# Revit family: BC_Hitachi_RASC-HNpE_LOD200
name_source: partatom
category: Equipement de génie climatique
revit_build: Autodesk Revit 2016 (Build: 20150220_1215(x64)
units: mm (PartAtom-declared; Revit-internal decimal feet)

## family parameters
Basée sur le plan de construction = Non
Cote de connecteur circulaire = Utiliser le diamètre
Couper avec des vides une fois chargée = Non
Numéro OmniClass = 23.75.00.00
Partagée = Non
Point de calcul de pièce = Non
Titre OmniClass = Climate Control (HVAC)
Toujours verticalement = Oui
Type d'élément = Normal

## types (5) — shared parameters
Description = Centrifugal VRF Series RASC-HNPE
Fabricant = HITACHI
Frequency = 50 Hz
Maximum AC Voltage = 440 V
Maximum Connected Capacity (%) = 120
Minimum AC Voltage = 360 V
Minimum Connected Capacity (%) = 75
Modèle = Outdoor Unit - Centrifugal RASC-HNPE
Nominal Voltage = 400 V
Number of Poles = 3
Refrigerant = R410A

## per-type parameters (varying)
- RASC-4HNPE: Coefficient Of Performance (COP)=3.8; Cooling Capacity=10 kW; Distance from left outlet=123 mm; ESEER=6.65; Energy Efficiency Ratio (EER)=3.35; Gas Diameter=16 mm; Heating Capacity=11 kW; Height Gas pipe=439 mm; Height liquid pipe=319 mm; Input Height=444 mm; Input Width=642 mm; Liquid Diameter=10 mm  [stored 0.0328084 ft]; Mass=192.00 kg; Maximum Air Flow=55000.0 L/min; Maximum Input Power=9 kW; Nominal Current=14 A; Nominal cooling power input=3 kW; Nominal heating power input=3 kW; Output Height=288 mm; Output Width=334 mm; Overall Depth=1015 mm; Overall Height=575 mm; Overall Width=1415 mm; Product Code=7E343107; Recommended circuit breaker=20 A; Refrigerant charge=4.10 kg; Running current cooling=5 A; Running current heating=5 A; Sound power dB(A)=70; Sound pressure level Night mode cooling (dB(A))=48; Sound pressure level cooling (dB(A))=52; Sound pressure level heating (dB(A))=53; Space between inlet outlet=222 mm; Static Pressure Maximum=90.0 Pa; Static Pressure Nominal=56.0 Pa
- RASC-5HNPE: Coefficient Of Performance (COP)=3.4; Cooling Capacity=13 kW; Distance from left outlet=123 mm; ESEER=6.41; Energy Efficiency Ratio (EER)=3.14; Gas Diameter=16 mm; Heating Capacity=14 kW; Height Gas pipe=439 mm; Height liquid pipe=319 mm; Input Height=444 mm; Input Width=642 mm; Liquid Diameter=10 mm  [stored 0.0328084 ft]; Mass=192.00 kg; Maximum Air Flow=60000.0 L/min; Maximum Input Power=9 kW; Nominal Current=14 A; Nominal cooling power input=4 kW; Nominal heating power input=4 kW; Output Height=288 mm; Output Width=334 mm; Overall Depth=1015 mm; Overall Height=575 mm; Overall Width=1415 mm; Product Code=7E343108; Recommended circuit breaker=20 A; Refrigerant charge=4.20 kg; Running current cooling=6 A; Running current heating=7 A; Sound power dB(A)=71; Sound pressure level Night mode cooling (dB(A))=48; Sound pressure level cooling (dB(A))=52; Sound pressure level heating (dB(A))=53; Space between inlet outlet=222 mm; Static Pressure Maximum=100.0 Pa; Static Pressure Nominal=72.0 Pa
- RASC-6HNPE: Coefficient Of Performance (COP)=2.7; Cooling Capacity=14 kW; Distance from left outlet=123 mm; ESEER=6.19; Energy Efficiency Ratio (EER)=2.75; Gas Diameter=16 mm; Heating Capacity=16 kW; Height Gas pipe=439 mm; Height liquid pipe=319 mm; Input Height=444 mm; Input Width=642 mm; Liquid Diameter=10 mm  [stored 0.0328084 ft]; Mass=192.00 kg; Maximum Air Flow=60000.0 L/min; Maximum Input Power=10 kW; Nominal Current=16 A; Nominal cooling power input=5 kW; Nominal heating power input=6 kW; Output Height=288 mm; Output Width=334 mm; Overall Depth=1015 mm; Overall Height=575 mm; Overall Width=1415 mm; Product Code=7E343109; Recommended circuit breaker=20 A; Refrigerant charge=4.20 kg; Running current cooling=8 A; Running current heating=9 A; Sound power dB(A)=72; Sound pressure level Night mode cooling (dB(A))=49; Sound pressure level cooling (dB(A))=53; Sound pressure level heating (dB(A))=54; Space between inlet outlet=222 mm; Static Pressure Maximum=100.0 Pa; Static Pressure Nominal=100.0 Pa
- RASC-8HNPE: Coefficient Of Performance (COP)=3.2; Cooling Capacity=20 kW; Distance from left outlet=188 mm  [stored 0.616798 ft]; ESEER=6.15; Energy Efficiency Ratio (EER)=2.7; Gas Diameter=25 mm  [stored 0.082021 ft]; Heating Capacity=22 kW; Height Gas pipe=504 mm  [stored 1.65354 ft]; Height liquid pipe=391 mm; Input Height=509 mm  [stored 1.66995 ft]; Input Width=925 mm  [stored 3.03478 ft]; Liquid Diameter=10 mm  [stored 0.0328084 ft]; Mass=300.00 kg; Maximum Air Flow=115000.0 L/min; Maximum Input Power=15 kW; Nominal Current=25 A; Nominal cooling power input=7 kW; Nominal heating power input=7 kW; Output Height=337 mm  [stored 1.10564 ft]; Output Width=398 mm  [stored 1.30577 ft]; Overall Depth=1360 mm  [stored 4.46194 ft]; Overall Height=640 mm  [stored 2.09974 ft]; Overall Width=1850 mm  [stored 6.06955 ft]; Product Code=7E343110; Recommended circuit breaker=30 A; Refrigerant charge=5.70 kg; Running current cooling=12 A; Running current heating=11 A; Sound power dB(A)=74; Sound pressure level Night mode cooling (dB(A))=51; Sound pressure level cooling (dB(A))=55; Sound pressure level heating (dB(A))=56; Space between inlet outlet=245 mm  [stored 0.803806 ft]; Static Pressure Maximum=120.0 Pa; Static Pressure Nominal=84.0 Pa
- RASC-10HNPE: Coefficient Of Performance (COP)=3.05; Cooling Capacity=24 kW; Distance from left outlet=188 mm  [stored 0.616798 ft]; ESEER=6.13; Energy Efficiency Ratio (EER)=2.66; Gas Diameter=25 mm  [stored 0.082021 ft]; Heating Capacity=26 kW; Height Gas pipe=504 mm  [stored 1.65354 ft]; Height liquid pipe=391 mm; Input Height=509 mm  [stored 1.66995 ft]; Input Width=925 mm  [stored 3.03478 ft]; Liquid Diameter=13 mm; Mass=303.00 kg; Maximum Air Flow=115000.0 L/min; Maximum Input Power=15 kW; Nominal Current=25 A; Nominal cooling power input=9 kW; Nominal heating power input=9 kW; Output Height=337 mm  [stored 1.10564 ft]; Output Width=398 mm  [stored 1.30577 ft]; Overall Depth=1360 mm  [stored 4.46194 ft]; Overall Height=640 mm  [stored 2.09974 ft]; Overall Width=1850 mm  [stored 6.06955 ft]; Product Code=7E343111; Recommended circuit breaker=30 A; Refrigerant charge=6.20 kg; Running current cooling=15 A; Running current heating=14 A; Sound power dB(A)=75; Sound pressure level Night mode cooling (dB(A))=52; Sound pressure level cooling (dB(A))=56; Sound pressure level heating (dB(A))=57; Space between inlet outlet=245 mm  [stored 0.803806 ft]; Static Pressure Maximum=120.0 Pa; Static Pressure Nominal=102.0 Pa

note: column(s) folded — value = type name in every type: Commentaires du type

note: [stored X ft] marks values corroborated as IEEE doubles in the binary element streams (Revit-internal decimal feet)

## geometry (parser evidence)
native form markers: Blend x2
no freeform markers — native parametric forms only
